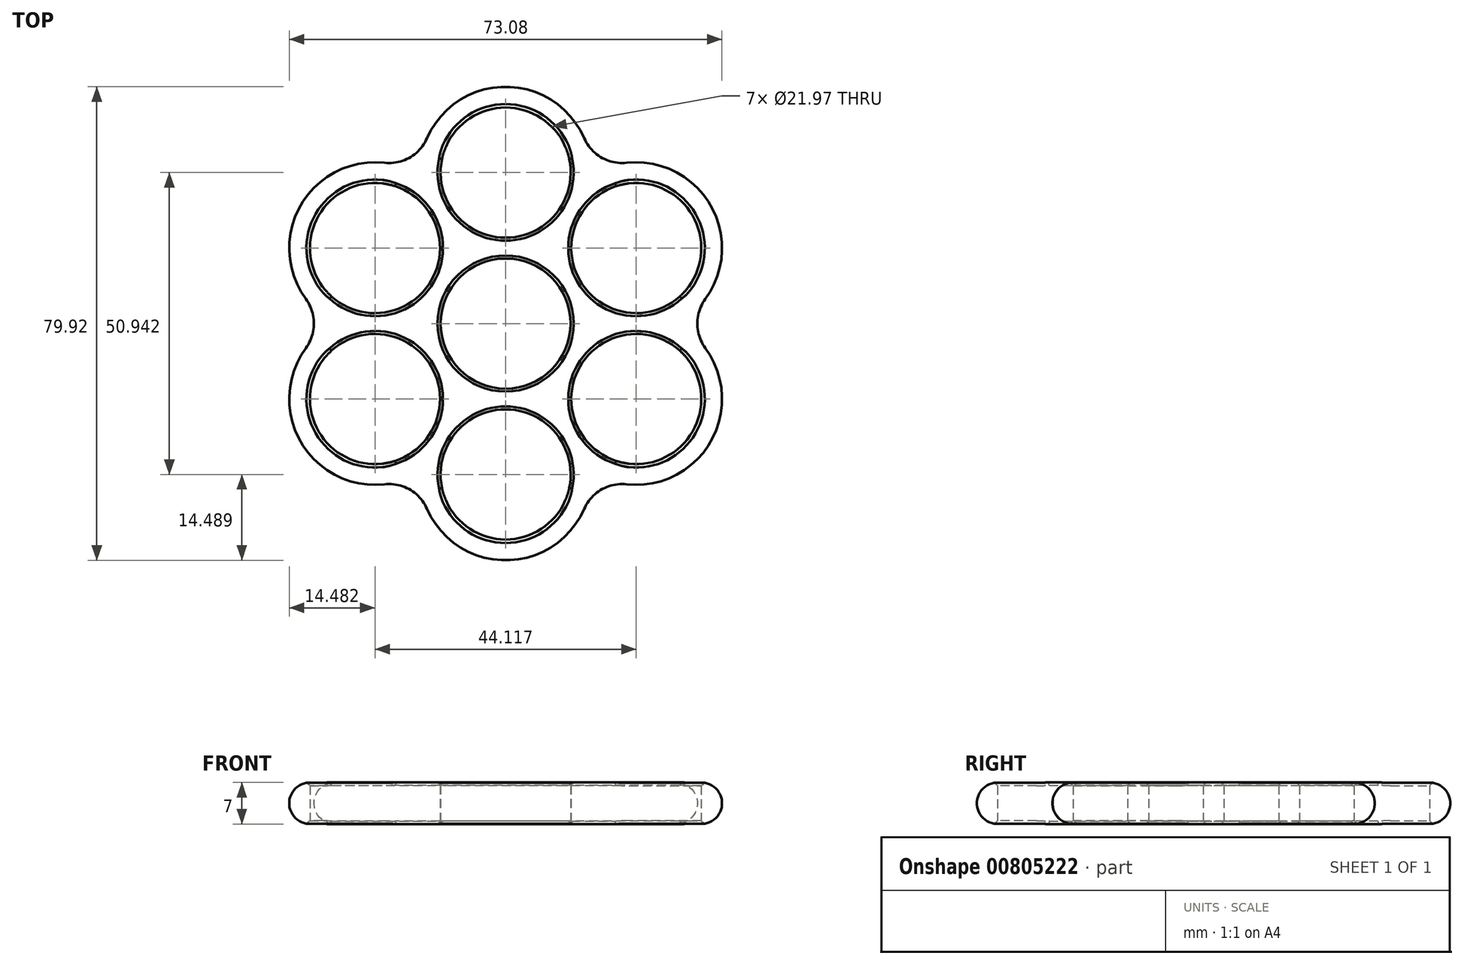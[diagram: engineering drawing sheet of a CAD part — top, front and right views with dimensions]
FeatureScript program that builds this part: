
annotation { "Feature Type Name" : "Feature", "Feature Type Description" : "" }
export const myFeature = defineFeature(function(context is Context, id is Id, definition is map)
    precondition{}
    {
        {
            var Q0;
            Q0=qCreatedBy(makeId("Top.planeOp"),FACE);
            var sketch = newSketch(context, id + "F0", { "sketchPlane" : qUnion([Q0])});
            skCircle(sketch, "E0", {"center": v(0, 0) * mm, "radius": 10.99 * mm});
            skCircle(sketch, "E1", {"center": v(0, 25.47) * mm, "radius": 10.99 * mm});
            skArc(sketch, "E2", {"start": v(0, 25.47) * mm, "mid": v(-22.06, 12.74) * mm, "end": v(-22.06, -12.74) * mm, "construction": true});
            skArc(sketch, "E3", {"start": v(-22.06, -12.74) * mm, "mid": v(0, -25.47) * mm, "end": v(22.06, -12.74) * mm, "construction": true});
            skArc(sketch, "E4", {"start": v(22.06, -12.74) * mm, "mid": v(22.06, 12.74) * mm, "end": v(0, 25.47) * mm, "construction": true});
            skCircle(sketch, "E5", {"center": v(22.06, -12.74) * mm, "radius": 10.99 * mm});
            skLineSegment(sketch, "E6", {"start": v(-22.06, -12.74) * mm, "end": v(0, 25.47) * mm, "construction": true});
            skLineSegment(sketch, "E7", {"start": v(22.06, -12.74) * mm, "end": v(0, 25.47) * mm, "construction": true});
            skLineSegment(sketch, "E8", {"start": v(-22.06, -12.74) * mm, "end": v(22.06, -12.74) * mm, "construction": true});
            skPoint(sketch, "E9.visualSharp", {"position": v(-14.48, -0.4) * mm});
            skPoint(sketch, "E10.visualSharp", {"position": v(-7.58, -12.35) * mm});
            skPoint(sketch, "E11.visualSharp", {"position": v(7.58, -12.35) * mm});
            skPoint(sketch, "E12.visualSharp", {"position": v(14.48, -0.4) * mm});
            skPoint(sketch, "E13.visualSharp", {"position": v(6.9, 12.74) * mm});
            skPoint(sketch, "E14.visualSharp", {"position": v(-6.9, 12.74) * mm});
            skLineSegment(sketch, "E15.trimOffspring", {"start": v(-32.82, -3.04) * mm, "end": v(-32.82, -3.04) * mm});
            skLineSegment(sketch, "E16.trimOffspring", {"start": v(-10.23, 15.21) * mm, "end": v(-10.23, 15.21) * mm});
            skLineSegment(sketch, "E17.trimOffspring", {"start": v(13.78, 29.94) * mm, "end": v(13.78, 29.94) * mm});
            skLineSegment(sketch, "E18.trimOffspring", {"start": v(18.29, 1.25) * mm, "end": v(18.29, 1.25) * mm});
            skLineSegment(sketch, "E19.trimOffspring", {"start": v(19.04, -26.9) * mm, "end": v(19.04, -26.9) * mm});
            skPoint(sketch, "E20.visualSharp", {"position": v(13.78, 29.94) * mm});
            skLineSegment(sketch, "E21", {"start": v(-22.06, 12.74) * mm, "end": v(22.06, 12.74) * mm, "construction": true});
            skLineSegment(sketch, "E22", {"start": v(22.06, 12.74) * mm, "end": v(0, -25.47) * mm, "construction": true});
            skLineSegment(sketch, "E23", {"start": v(0, -25.47) * mm, "end": v(-22.06, 12.74) * mm, "construction": true});
            skCircle(sketch, "E24", {"center": v(-22.06, 12.74) * mm, "radius": 10.99 * mm});
            skCircle(sketch, "E25", {"center": v(22.06, 12.74) * mm, "radius": 10.99 * mm});
            skCircle(sketch, "E26", {"center": v(-22.06, -12.74) * mm, "radius": 10.99 * mm});
            skCircle(sketch, "E27", {"center": v(0, -25.47) * mm, "radius": 10.99 * mm});
            skArc(sketch, "E28.0", {"start": v(14.48, 25.08) * mm, "mid": v(0, 39.96) * mm, "end": v(-14.48, 25.08) * mm});
            skArc(sketch, "E29.0", {"start": v(28.96, 0) * mm, "mid": v(34.6, 19.98) * mm, "end": v(14.48, 25.08) * mm});
            skArc(sketch, "E30.0", {"start": v(-28.96, 0) * mm, "mid": v(-34.6, -19.98) * mm, "end": v(-14.48, -25.08) * mm});
            skArc(sketch, "E31.trimOffspring", {"start": v(-14.48, 25.08) * mm, "mid": v(-34.6, 19.98) * mm, "end": v(-28.96, 0) * mm});
            skArc(sketch, "E32.trimOffspring", {"start": v(14.48, -25.08) * mm, "mid": v(34.6, -19.98) * mm, "end": v(28.96, 0) * mm});
            skArc(sketch, "E33.trimOffspring", {"start": v(-14.48, -25.08) * mm, "mid": v(0, -39.96) * mm, "end": v(14.48, -25.08) * mm});
            skSolve(sketch);
        }
        {
            var Q0;
            Q0 = qSketchRegion(id + "F0", true);
            extrude(context, id + "F1", {"entities" : qUnion([Q0]), "depth" : 7 * mm, "offsetDistance" : 25.4 * mm});
        }
        {
            var Q0;
            Q0=makeQuery(id+"F1.opExtrude","SWEPT_EDGE",EDGE,{"disambiguationData":[OSD([sQuery(id+"F0.wireOp",EDGE,"E32.trimOffspring"),sQuery(id+"F0.wireOp",EDGE,"E33.trimOffspring")])]});
            var Q1;
            Q1=makeQuery(id+"F1.opExtrude","SWEPT_EDGE",EDGE,{"disambiguationData":[OSD([sQuery(id+"F0.wireOp",EDGE,"E29.0"),sQuery(id+"F0.wireOp",EDGE,"E32.trimOffspring")])]});
            var Q2;
            Q2=makeQuery(id+"F1.opExtrude","SWEPT_EDGE",EDGE,{"disambiguationData":[OSD([sQuery(id+"F0.wireOp",EDGE,"E28.0"),sQuery(id+"F0.wireOp",EDGE,"E29.0")])]});
            var Q3;
            Q3=makeQuery(id+"F1.opExtrude","SWEPT_EDGE",EDGE,{"disambiguationData":[OSD([sQuery(id+"F0.wireOp",EDGE,"E28.0"),sQuery(id+"F0.wireOp",EDGE,"E31.trimOffspring")])]});
            var Q4;
            Q4=makeQuery(id+"F1.opExtrude","SWEPT_EDGE",EDGE,{"disambiguationData":[OSD([sQuery(id+"F0.wireOp",EDGE,"E30.0"),sQuery(id+"F0.wireOp",EDGE,"E31.trimOffspring")])]});
            var Q5;
            Q5=makeQuery(id+"F1.opExtrude","SWEPT_EDGE",EDGE,{"disambiguationData":[OSD([sQuery(id+"F0.wireOp",EDGE,"E30.0"),sQuery(id+"F0.wireOp",EDGE,"E33.trimOffspring")])]});
            fillet(context, id + "F2", {"entities" : qUnion([Q0, Q1, Q2, Q3, Q4, Q5]), "radius" : 7 * mm, "tangentPropagation" : true, "allowEdgeOverflow" : false});
        }
        {
            var Q0;
            Q0=makeQuery(id+"F1.opExtrude","CAP_EDGE",EDGE,{"disambiguationData":[OSD([sQuery(id+"F0.wireOp",EDGE,"E30.0")])],"isStart":false});
            var Q1;
            {var subQ0=sQuery(id+"F0.wireOp",EDGE,"E33.trimOffspring");var subQ1=sQuery(id+"F0.wireOp",EDGE,"E30.0");Q1=makeQuery(id+"F2.opFillet","BLEND_EDGE",EDGE,{"blendedFrom":[makeQuery(id+"F1.opExtrude","SWEPT_EDGE",EDGE,{"disambiguationData":[OSD([subQ1,subQ0])]}),makeQuery(id+"F1.opExtrude","CAP_FACE",FACE,{"disambiguationData":[OSD([sQuery(id+"F0.wireOp",EDGE,"E0"),sQuery(id+"F0.wireOp",EDGE,"E1"),sQuery(id+"F0.wireOp",EDGE,"E5"),sQuery(id+"F0.wireOp",EDGE,"E24"),sQuery(id+"F0.wireOp",EDGE,"E25"),sQuery(id+"F0.wireOp",EDGE,"E26"),sQuery(id+"F0.wireOp",EDGE,"E27"),sQuery(id+"F0.wireOp",EDGE,"E28.0"),sQuery(id+"F0.wireOp",EDGE,"E29.0"),subQ1,sQuery(id+"F0.wireOp",EDGE,"E31.trimOffspring"),sQuery(id+"F0.wireOp",EDGE,"E32.trimOffspring"),subQ0])],"isStart":true})],"blendedInto":[makeQuery(id+"F1.opExtrude","CAP_FACE",FACE,{"disambiguationData":[OSD([sQuery(id+"F0.wireOp",EDGE,"E0"),sQuery(id+"F0.wireOp",EDGE,"E1"),sQuery(id+"F0.wireOp",EDGE,"E5"),sQuery(id+"F0.wireOp",EDGE,"E24"),sQuery(id+"F0.wireOp",EDGE,"E25"),sQuery(id+"F0.wireOp",EDGE,"E26"),sQuery(id+"F0.wireOp",EDGE,"E27"),sQuery(id+"F0.wireOp",EDGE,"E28.0"),sQuery(id+"F0.wireOp",EDGE,"E29.0"),subQ1,sQuery(id+"F0.wireOp",EDGE,"E31.trimOffspring"),sQuery(id+"F0.wireOp",EDGE,"E32.trimOffspring"),subQ0])],"isStart":true})]});}
            fillet(context, id + "F3", {"entities" : qUnion([Q0, Q1]), "radius" : 3.5 * mm, "tangentPropagation" : true, "allowEdgeOverflow" : false});
        }
        {
            var Q0;
            Q0=makeQuery(id+"F3.opFillet","BLEND_EDGE",EDGE,{"blendedFrom":[makeQuery(id+"F1.opExtrude","CAP_EDGE",EDGE,{"disambiguationData":[OSD([sQuery(id+"F0.wireOp",EDGE,"824bbc60-00f9-4c88-a136-10df3727da02.0")])],"isStart":false}),makeQuery(id+"F1.opExtrude","SWEPT_FACE",FACE,{"disambiguationData":[OSD([sQuery(id+"F0.wireOp",EDGE,"ykTur6Wy-KAEY-Ysq0-AObf-bR51JLOCaOPN")])]})],"blendedInto":[makeQuery(id+"F1.opExtrude","SWEPT_FACE",FACE,{"disambiguationData":[OSD([sQuery(id+"F0.wireOp",EDGE,"ykTur6Wy-KAEY-Ysq0-AObf-bR51JLOCaOPN")])]})]});
            var Q1;
            Q1=makeQuery(id+"F1.opExtrude","CAP_EDGE",EDGE,{"disambiguationData":[OSD([sQuery(id+"F0.wireOp",EDGE,"E0")])],"isStart":false});
            var Q2;
            Q2=makeQuery(id+"F3.opFillet","BLEND_EDGE",EDGE,{"blendedFrom":[makeQuery(id+"F1.opExtrude","CAP_EDGE",EDGE,{"disambiguationData":[OSD([sQuery(id+"F0.wireOp",EDGE,"579bf34d-a0d7-49ba-83c9-b9f074fa5f16.0")])],"isStart":false}),makeQuery(id+"F1.opExtrude","SWEPT_FACE",FACE,{"disambiguationData":[OSD([sQuery(id+"F0.wireOp",EDGE,"E1")])]})],"blendedInto":[makeQuery(id+"F1.opExtrude","SWEPT_FACE",FACE,{"disambiguationData":[OSD([sQuery(id+"F0.wireOp",EDGE,"E1")])]})]});
            var Q3;
            Q3=makeQuery(id+"F1.opExtrude","CAP_EDGE",EDGE,{"disambiguationData":[OSD([sQuery(id+"F0.wireOp",EDGE,"E5")])],"isStart":false});
            var Q4;
            Q4=makeQuery(id+"F1.opExtrude","CAP_EDGE",EDGE,{"disambiguationData":[OSD([sQuery(id+"F0.wireOp",EDGE,"E5")])],"isStart":true});
            var Q5;
            Q5=makeQuery(id+"F3.opFillet","BLEND_EDGE",EDGE,{"blendedFrom":[makeQuery(id+"F1.opExtrude","CAP_EDGE",EDGE,{"disambiguationData":[OSD([sQuery(id+"F0.wireOp",EDGE,"a1778e8f-b680-4088-aae0-ead9d217816b.trimOffspring")])],"isStart":true}),makeQuery(id+"F1.opExtrude","SWEPT_FACE",FACE,{"disambiguationData":[OSD([sQuery(id+"F0.wireOp",EDGE,"E0")])]})],"blendedInto":[makeQuery(id+"F1.opExtrude","SWEPT_FACE",FACE,{"disambiguationData":[OSD([sQuery(id+"F0.wireOp",EDGE,"E0")])]})]});
            var Q6;
            Q6=makeQuery(id+"F1.opExtrude","CAP_EDGE",EDGE,{"disambiguationData":[OSD([sQuery(id+"F0.wireOp",EDGE,"ykTur6Wy-KAEY-Ysq0-AObf-bR51JLOCaOPN")])],"isStart":true});
            var Q7;
            Q7=makeQuery(id+"F3.opFillet","BLEND_EDGE",EDGE,{"blendedFrom":[makeQuery(id+"F1.opExtrude","CAP_EDGE",EDGE,{"disambiguationData":[OSD([sQuery(id+"F0.wireOp",EDGE,"579bf34d-a0d7-49ba-83c9-b9f074fa5f16.0")])],"isStart":true}),makeQuery(id+"F1.opExtrude","SWEPT_FACE",FACE,{"disambiguationData":[OSD([sQuery(id+"F0.wireOp",EDGE,"E1")])]})],"blendedInto":[makeQuery(id+"F1.opExtrude","SWEPT_FACE",FACE,{"disambiguationData":[OSD([sQuery(id+"F0.wireOp",EDGE,"E1")])]})]});
            var Q8;
            Q8=makeQuery(id+"F1.opExtrude","CAP_EDGE",EDGE,{"disambiguationData":[OSD([sQuery(id+"F0.wireOp",EDGE,"E27")])],"isStart":false});
            var Q9;
            Q9=makeQuery(id+"F1.opExtrude","CAP_EDGE",EDGE,{"disambiguationData":[OSD([sQuery(id+"F0.wireOp",EDGE,"E26")])],"isStart":false});
            var Q10;
            Q10=makeQuery(id+"F1.opExtrude","CAP_EDGE",EDGE,{"disambiguationData":[OSD([sQuery(id+"F0.wireOp",EDGE,"E24")])],"isStart":false});
            var Q11;
            Q11=makeQuery(id+"F1.opExtrude","CAP_EDGE",EDGE,{"disambiguationData":[OSD([sQuery(id+"F0.wireOp",EDGE,"E1")])],"isStart":false});
            var Q12;
            Q12=makeQuery(id+"F1.opExtrude","CAP_EDGE",EDGE,{"disambiguationData":[OSD([sQuery(id+"F0.wireOp",EDGE,"E25")])],"isStart":false});
            var Q13;
            Q13=makeQuery(id+"F1.opExtrude","CAP_EDGE",EDGE,{"disambiguationData":[OSD([sQuery(id+"F0.wireOp",EDGE,"E24")])],"isStart":true});
            var Q14;
            Q14=makeQuery(id+"F1.opExtrude","CAP_EDGE",EDGE,{"disambiguationData":[OSD([sQuery(id+"F0.wireOp",EDGE,"E26")])],"isStart":true});
            var Q15;
            Q15=makeQuery(id+"F1.opExtrude","CAP_EDGE",EDGE,{"disambiguationData":[OSD([sQuery(id+"F0.wireOp",EDGE,"E27")])],"isStart":true});
            var Q16;
            Q16=makeQuery(id+"F1.opExtrude","CAP_EDGE",EDGE,{"disambiguationData":[OSD([sQuery(id+"F0.wireOp",EDGE,"E0")])],"isStart":true});
            var Q17;
            Q17=makeQuery(id+"F1.opExtrude","CAP_EDGE",EDGE,{"disambiguationData":[OSD([sQuery(id+"F0.wireOp",EDGE,"E1")])],"isStart":true});
            var Q18;
            Q18=makeQuery(id+"F1.opExtrude","CAP_EDGE",EDGE,{"disambiguationData":[OSD([sQuery(id+"F0.wireOp",EDGE,"E25")])],"isStart":true});
            chamfer(context, id + "F4", {"entities" : qUnion([Q0, Q1, Q2, Q3, Q4, Q5, Q6, Q7, Q8, Q9, Q10, Q11, Q12, Q13, Q14, Q15, Q16, Q17, Q18]), "width" : .5 * mm, "tangentPropagation" : true});
        }
    });
